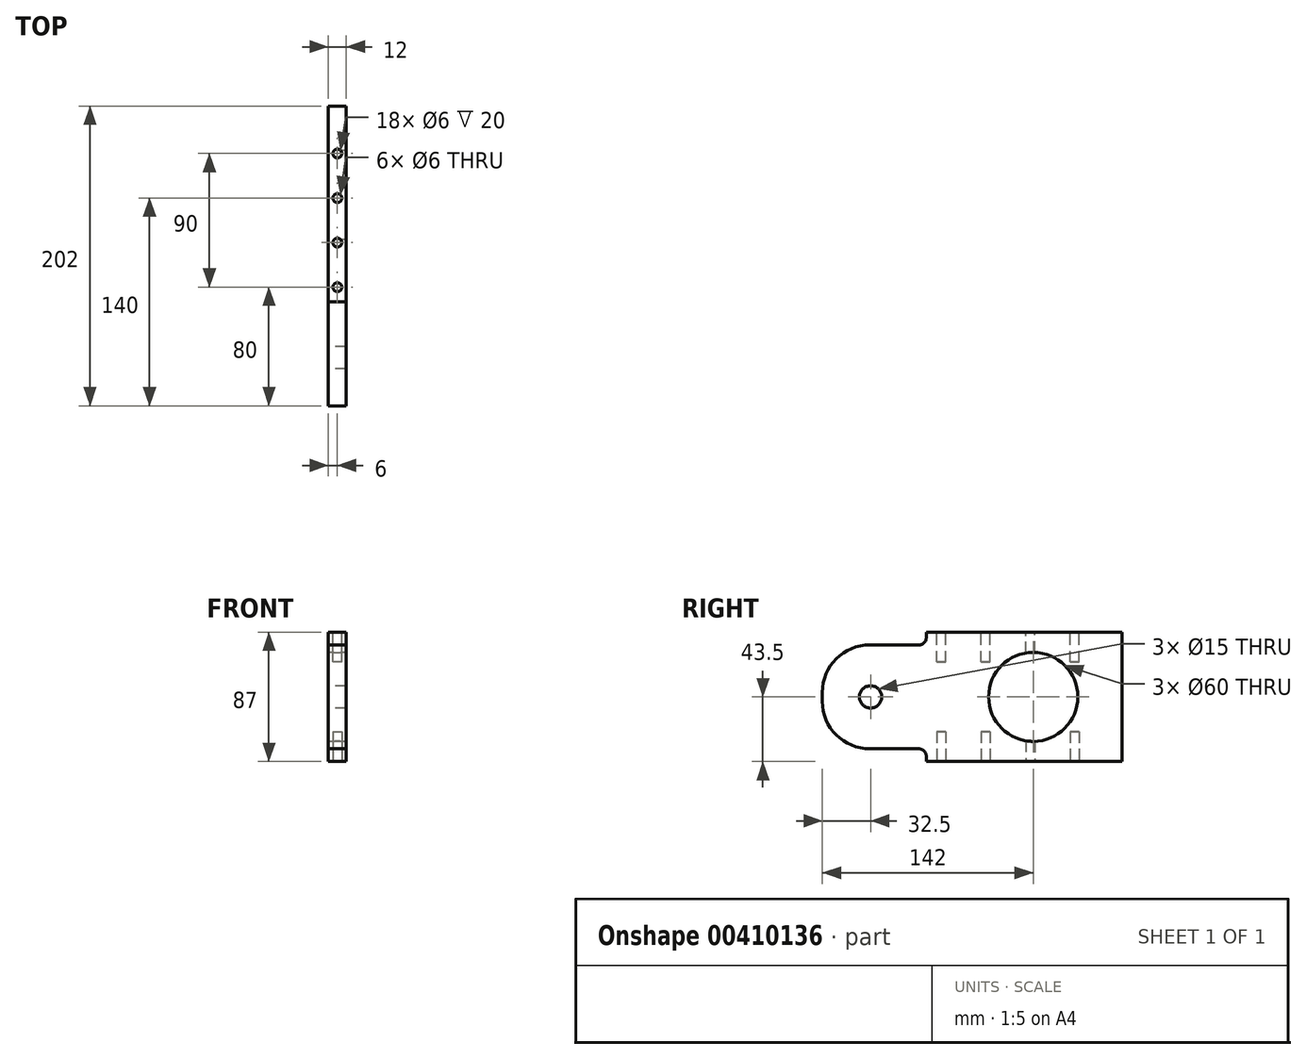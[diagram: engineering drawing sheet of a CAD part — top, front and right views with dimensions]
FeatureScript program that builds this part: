
annotation { "Feature Type Name" : "Feature", "Feature Type Description" : "" }
export const myFeature = defineFeature(function(context is Context, id is Id, definition is map)
    precondition{}
    {
        {
            var Q0;
            Q0=qCreatedBy(makeId("Right.planeOp"),FACE);
            var sketch = newSketch(context, id + "F0", { "sketchPlane" : qUnion([Q0])});
            skLineSegment(sketch, "E0.bottom", {"start": v(32, 0) * mm, "end": v(65, 0) * mm});
            skLineSegment(sketch, "E0.top", {"start": v(32, 70) * mm, "end": v(65, 70) * mm});
            skLineSegment(sketch, "E0.left", {"start": v(0, 32) * mm, "end": v(0, 38) * mm});
            skLineSegment(sketch, "E1", {"start": v(0, 35) * mm, "end": v(202, 35) * mm, "construction": true});
            skCircle(sketch, "E2", {"center": v(32.5, 35) * mm, "radius": 7.5 * mm});
            skPoint(sketch, "E3.visualSharp", {"position": v(0, 70) * mm});
            skArc(sketch, "E3.filletArc", {"start": v(32, 70) * mm, "mid": v(9.37, 60.63) * mm, "end": v(0, 38) * mm});
            skPoint(sketch, "E4.visualSharp", {"position": v(0, 0) * mm});
            skArc(sketch, "E4.filletArc", {"start": v(0, 32) * mm, "mid": v(9.37, 9.37) * mm, "end": v(32, 0) * mm});
            skLineSegment(sketch, "E5.bottom", {"start": v(202, 78.5) * mm, "end": v(70, 78.5) * mm});
            skLineSegment(sketch, "E5.top", {"start": v(202, -8.5) * mm, "end": v(70, -8.5) * mm});
            skLineSegment(sketch, "E5.left", {"start": v(202, 78.5) * mm, "end": v(202, -8.5) * mm});
            skLineSegment(sketch, "E5.right", {"start": v(70, 78.5) * mm, "end": v(70, 75) * mm});
            skArc(sketch, "E6.filletArc", {"start": v(65, 70) * mm, "mid": v(68.54, 71.46) * mm, "end": v(70, 75) * mm});
            skLineSegment(sketch, "E7", {"start": v(70, -5) * mm, "end": v(70, -8.5) * mm});
            skPoint(sketch, "E8.visualSharp", {"position": v(70, 0) * mm});
            skArc(sketch, "E8.filletArc", {"start": v(70, -5) * mm, "mid": v(68.54, -1.46) * mm, "end": v(65, 0) * mm});
            skLineSegment(sketch, "E9", {"start": v(70, 78.5) * mm, "end": v(70, -8.5) * mm, "construction": true});
            skCircle(sketch, "E10", {"center": v(142, 35) * mm, "radius": 30 * mm});
            skSolve(sketch);
        }
        {
            var Q0;
            Q0=qSketchRegion(id+"F0",true);
            extrude(context, id + "F1", {"entities" : qUnion([Q0]), "depth" : 12 * mm});
        }
        {
            var Q0;
            Q0=makeQuery(id+"F1.opExtrude","SWEPT_FACE",FACE,{"disambiguationData":[OSD([sQuery(id+"F0.wireOp",EDGE,"E5.bottom")])]});
            var sketch = newSketch(context, id + "F2", { "sketchPlane" : qUnion([Q0])});
            skLineSegment(sketch, "E11", {"start": v(6, 202) * mm, "end": v(6, 70) * mm, "construction": true});
            skCircle(sketch, "E12", {"center": v(6, 80) * mm, "radius": 3 * mm});
            skCircle(sketch, "E13.0.1.0", {"center": v(6, 110) * mm, "radius": 3 * mm});
            skCircle(sketch, "E13.0.2.0", {"center": v(6, 140) * mm, "radius": 3 * mm});
            skCircle(sketch, "E13.0.3.0", {"center": v(6, 170) * mm, "radius": 3 * mm});
            skLineSegment(sketch, "E13.direction1", {"start": v(6, 80) * mm, "end": v(31, 80) * mm, "construction": true});
            skLineSegment(sketch, "E13.direction2", {"start": v(6, 80) * mm, "end": v(6, 110) * mm, "construction": true});
            skSolve(sketch);
        }
        {
            var Q0;
            Q0 = qSketchRegion(id + "F2", true);
            extrude(context, id + "F3", {"entities" : qUnion([Q0]), "operationType" : NewBodyOperationType.REMOVE, "oppositeDirection" : true, "depth" : 20 * mm});
        }
        {
            var Q0;
            Q0=makeQuery(id+"F1.opExtrude","SWEPT_FACE",FACE,{"disambiguationData":[OSD([sQuery(id+"F0.wireOp",EDGE,"E5.top")])]});
            var sketch = newSketch(context, id + "F4", { "sketchPlane" : qUnion([Q0])});
            skLineSegment(sketch, "E14.0", {"start": v(6, -202) * mm, "end": v(6, -70) * mm});
            skCircle(sketch, "E14.1", {"center": v(6, -80) * mm, "radius": 3 * mm});
            skCircle(sketch, "E14.2", {"center": v(6, -110) * mm, "radius": 3 * mm});
            skCircle(sketch, "E14.3", {"center": v(6, -140) * mm, "radius": 3 * mm});
            skCircle(sketch, "E14.4", {"center": v(6, -170) * mm, "radius": 3 * mm});
            skLineSegment(sketch, "E14.5", {"start": v(6, -80) * mm, "end": v(31, -80) * mm});
            skLineSegment(sketch, "E14.6", {"start": v(6, -80) * mm, "end": v(6, -110) * mm});
            skSolve(sketch);
        }
        {
            var Q0;
            Q0 = qSketchRegion(id + "F4", true);
            extrude(context, id + "F5", {"entities" : qUnion([Q0]), "operationType" : NewBodyOperationType.REMOVE, "oppositeDirection" : true, "depth" : 20 * mm});
        }
    });
